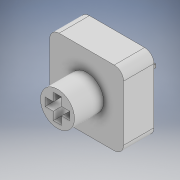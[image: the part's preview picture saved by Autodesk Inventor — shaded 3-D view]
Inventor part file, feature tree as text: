
AUTODESK INVENTOR PART (.ipt)
format: ipt  version: 2022 (Build 260153000, 153)  size: 246,784 bytes
history: native  units: in
note: dims shown in document units (in); Inventor stores cm internally (conversion verified against a paired STEP export)
features: sketch x4, extrude x3, plane x1, projected_geometry x1
ambient origin geometry x8: Origin, YZ Plane, XZ Plane, XY Plane, X Axis, Y Axis, Z Axis, Center Point
bodies: Body1 (feature_tree)
feature tree (9):
  sketch  "Sketch1"  dims[d3=0.2205in d4=0.1594in]
  plane  "Work Plane1"
  sketch  "Sketch2"  dims[d5=0.0531in d6=0.1594in]
  extrude  "Extrusion3"  Depth=0.1594in
  extrude  "Extrusion4"  Depth=0.1594in
  extrude  "Extrusion5"  Depth=0.5016in
  projected_geometry  "Projected Loop1"
  sketch  "Sketch3"  dims[d7=0.0531in d10=0.5016in]
  sketch  "Sketch4"  dims[d12=0.1969in d13=0.0in d14=0.2205in d15=0.1594in d16=0.0531in d17=0.1594in d18=0.0531in d19=0.189in d20=0.0in d21=0.0892in d22=0.2693in d23=0.0354in d24=0.0in]
